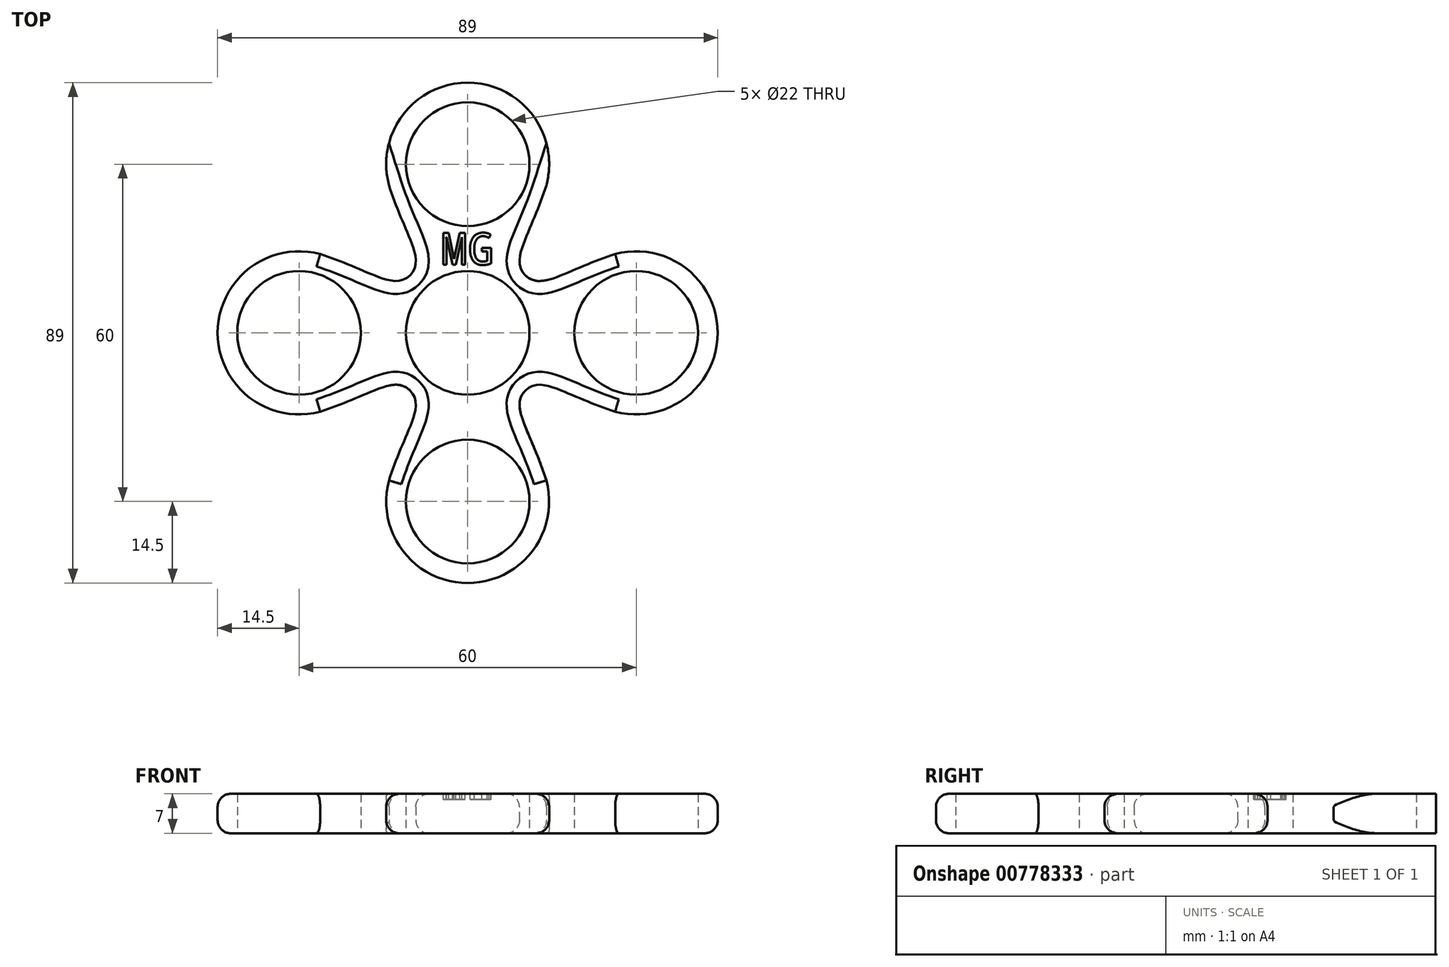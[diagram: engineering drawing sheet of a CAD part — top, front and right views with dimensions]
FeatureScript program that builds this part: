
annotation { "Feature Type Name" : "Feature", "Feature Type Description" : "" }
export const myFeature = defineFeature(function(context is Context, id is Id, definition is map)
    precondition{}
    {
        {
            var Q0;
            Q0=qCreatedBy(makeId("Top.planeOp"),FACE);
            var sketch = newSketch(context, id + "F0", { "sketchPlane" : qUnion([Q0])});
            skCircle(sketch, "E0", {"center": v(0, 0) * mm, "radius": 11 * mm});
            skCircle(sketch, "E1", {"center": v(0, 30) * mm, "radius": 11 * mm});
            skCircle(sketch, "E2", {"center": v(0, -30) * mm, "radius": 11 * mm});
            skCircle(sketch, "E3", {"center": v(30, 0) * mm, "radius": 11 * mm});
            skCircle(sketch, "E4", {"center": v(-30, 0) * mm, "radius": 11 * mm});
            skLineSegment(sketch, "E5", {"start": v(0, 0) * mm, "end": v(-49.5, 49.5) * mm, "construction": true});
            skLineSegment(sketch, "E6.MirrorCS", {"start": v(0, 0) * mm, "end": v(49.5, 49.5) * mm, "construction": true});
            skLineSegment(sketch, "E7.MirrorCS", {"start": v(0, 0) * mm, "end": v(49.5, -49.5) * mm, "construction": true});
            skLineSegment(sketch, "E8.MirrorCS", {"start": v(0, 0) * mm, "end": v(-49.5, -49.5) * mm, "construction": true});
            skArc(sketch, "E9", {"start": v(14, 26.25) * mm, "mid": v(0, 44.5) * mm, "end": v(-14, 26.25) * mm});
            skArc(sketch, "E10", {"start": v(26.25, -14) * mm, "mid": v(44.5, 0) * mm, "end": v(26.25, 14) * mm});
            skArc(sketch, "E11", {"start": v(-14, -26.25) * mm, "mid": v(0, -44.5) * mm, "end": v(14, -26.25) * mm});
            skArc(sketch, "E12", {"start": v(-26.25, 14) * mm, "mid": v(-44.5, 0) * mm, "end": v(-26.25, -14) * mm});
            skCircle(sketch, "E13", {"center": v(0, 0) * mm, "radius": 14.5 * mm, "construction": true});
            skLineSegment(sketch, "E14", {"start": v(0, 30) * mm, "end": v(-30, 0) * mm, "construction": true});
            skLineSegment(sketch, "E15", {"start": v(0, 30) * mm, "end": v(30, 0) * mm, "construction": true});
            skLineSegment(sketch, "E16", {"start": v(30, 0) * mm, "end": v(0, -30) * mm, "construction": true});
            skLineSegment(sketch, "E17", {"start": v(0, -30) * mm, "end": v(-30, 0) * mm, "construction": true});
            skFitSpline(sketch, "E18", {"points": [v(-14, 26.25) * mm, v(-10.25, 10.25) * mm], "startDerivative": vector(8.68, -26.95) * mm, "endDerivative": vector(-8.59, -8.59) * mm});
            skLineSegment(sketch, "E19", {"start": v(-10.25, 10.25) * mm, "end": v(-5.17, 15.34) * mm, "construction": true});
            skFitSpline(sketch, "E20.MirrorCS", {"points": [v(-26.25, 14) * mm, v(-10.25, 10.25) * mm], "startDerivative": vector(26.95, -8.68) * mm, "endDerivative": vector(8.59, 8.59) * mm});
            skFitSpline(sketch, "E21.MirrorCS", {"points": [v(14, 26.25) * mm, v(10.25, 10.25) * mm], "startDerivative": vector(-8.68, -26.95) * mm, "endDerivative": vector(8.59, -8.59) * mm});
            skArc(sketch, "E22.MirrorC", {"start": v(-14, 26.25) * mm, "mid": v(0, 44.5) * mm, "end": v(14, 26.25) * mm});
            skFitSpline(sketch, "E23.MirrorCS", {"points": [v(26.25, 14) * mm, v(10.25, 10.25) * mm], "startDerivative": vector(-26.95, -8.68) * mm, "endDerivative": vector(-8.59, 8.59) * mm});
            skFitSpline(sketch, "E24.MirrorCS", {"points": [v(26.25, -14) * mm, v(10.25, -10.25) * mm], "startDerivative": vector(-26.95, 8.68) * mm, "endDerivative": vector(-8.59, -8.59) * mm});
            skFitSpline(sketch, "E25.MirrorCS", {"points": [v(14, -26.25) * mm, v(10.25, -10.25) * mm], "startDerivative": vector(-8.68, 26.95) * mm, "endDerivative": vector(8.59, 8.59) * mm});
            skFitSpline(sketch, "E26.MirrorCS", {"points": [v(-14, -26.25) * mm, v(-10.25, -10.25) * mm], "startDerivative": vector(8.68, 26.95) * mm, "endDerivative": vector(-8.59, 8.59) * mm});
            skFitSpline(sketch, "E27.MirrorCS", {"points": [v(-26.25, -14) * mm, v(-10.25, -10.25) * mm], "startDerivative": vector(26.95, 8.68) * mm, "endDerivative": vector(8.59, -8.59) * mm});
            skSolve(sketch);
        }
        {
            var Q0;
            Q0=makeQuery(id+"F0.imprint","IMPRINT",FACE,{"disambiguationData":[TD([[makeQuery(id+"F0.imprint","IMPRINT",EDGE,{"derivedFrom":sQuery(id+"F0.wireOp",EDGE,"E0")}),-1.0]])]});
            extrude(context, id + "F1", {"entities" : qUnion([Q0]), "depth" : 7 * mm, "offsetDistance" : 25 * mm});
        }
        {
            var Q0;
            Q0=makeQuery(id+"F1.opExtrude","CAP_EDGE",EDGE,{"disambiguationData":[OSD([sQuery(id+"F0.wireOp",EDGE,"E27.MirrorCS")])],"isStart":false});
            var Q1;
            Q1=makeQuery(id+"F1.opExtrude","CAP_EDGE",EDGE,{"disambiguationData":[OSD([sQuery(id+"F0.wireOp",EDGE,"E20.MirrorCS")])],"isStart":false});
            var Q2;
            Q2=makeQuery(id+"F1.opExtrude","CAP_EDGE",EDGE,{"disambiguationData":[OSD([sQuery(id+"F0.wireOp",EDGE,"E12")])],"isStart":false});
            var Q3;
            Q3=makeQuery(id+"F1.opExtrude","CAP_EDGE",EDGE,{"disambiguationData":[OSD([sQuery(id+"F0.wireOp",EDGE,"E18")])],"isStart":false});
            var Q4;
            Q4=makeQuery(id+"F1.opExtrude","CAP_EDGE",EDGE,{"disambiguationData":[OSD([sQuery(id+"F0.wireOp",EDGE,"E21.MirrorCS")])],"isStart":false});
            var Q5;
            Q5=makeQuery(id+"F1.opExtrude","CAP_EDGE",EDGE,{"disambiguationData":[OSD([sQuery(id+"F0.wireOp",EDGE,"E23.MirrorCS")])],"isStart":false});
            var Q6;
            Q6=makeQuery(id+"F1.opExtrude","CAP_EDGE",EDGE,{"disambiguationData":[OSD([sQuery(id+"F0.wireOp",EDGE,"E24.MirrorCS")])],"isStart":false});
            var Q7;
            Q7=makeQuery(id+"F1.opExtrude","CAP_EDGE",EDGE,{"disambiguationData":[OSD([sQuery(id+"F0.wireOp",EDGE,"E25.MirrorCS")])],"isStart":false});
            var Q8;
            Q8=makeQuery(id+"F1.opExtrude","CAP_EDGE",EDGE,{"disambiguationData":[OSD([sQuery(id+"F0.wireOp",EDGE,"E10")])],"isStart":false});
            var Q9;
            Q9=makeQuery(id+"F1.opExtrude","CAP_EDGE",EDGE,{"disambiguationData":[OSD([sQuery(id+"F0.wireOp",EDGE,"E22.MirrorC")])],"isStart":false});
            var Q10;
            Q10=makeQuery(id+"F1.opExtrude","CAP_EDGE",EDGE,{"disambiguationData":[OSD([sQuery(id+"F0.wireOp",EDGE,"E26.MirrorCS")])],"isStart":false});
            var Q11;
            Q11=makeQuery(id+"F1.opExtrude","CAP_EDGE",EDGE,{"disambiguationData":[OSD([sQuery(id+"F0.wireOp",EDGE,"E11")])],"isStart":false});
            var Q12;
            Q12=makeQuery(id+"F1.opExtrude","CAP_EDGE",EDGE,{"disambiguationData":[OSD([sQuery(id+"F0.wireOp",EDGE,"E23.MirrorCS")])],"isStart":true});
            var Q13;
            Q13=makeQuery(id+"F1.opExtrude","CAP_EDGE",EDGE,{"disambiguationData":[OSD([sQuery(id+"F0.wireOp",EDGE,"E10")])],"isStart":true});
            var Q14;
            Q14=makeQuery(id+"F1.opExtrude","CAP_EDGE",EDGE,{"disambiguationData":[OSD([sQuery(id+"F0.wireOp",EDGE,"E24.MirrorCS")])],"isStart":true});
            var Q15;
            Q15=makeQuery(id+"F1.opExtrude","CAP_EDGE",EDGE,{"disambiguationData":[OSD([sQuery(id+"F0.wireOp",EDGE,"E25.MirrorCS")])],"isStart":true});
            var Q16;
            Q16=makeQuery(id+"F1.opExtrude","CAP_EDGE",EDGE,{"disambiguationData":[OSD([sQuery(id+"F0.wireOp",EDGE,"E11")])],"isStart":true});
            var Q17;
            Q17=makeQuery(id+"F1.opExtrude","CAP_EDGE",EDGE,{"disambiguationData":[OSD([sQuery(id+"F0.wireOp",EDGE,"E26.MirrorCS")])],"isStart":true});
            var Q18;
            Q18=makeQuery(id+"F1.opExtrude","CAP_EDGE",EDGE,{"disambiguationData":[OSD([sQuery(id+"F0.wireOp",EDGE,"E27.MirrorCS")])],"isStart":true});
            var Q19;
            Q19=makeQuery(id+"F1.opExtrude","CAP_EDGE",EDGE,{"disambiguationData":[OSD([sQuery(id+"F0.wireOp",EDGE,"E12")])],"isStart":true});
            var Q20;
            Q20=makeQuery(id+"F1.opExtrude","CAP_EDGE",EDGE,{"disambiguationData":[OSD([sQuery(id+"F0.wireOp",EDGE,"E20.MirrorCS")])],"isStart":true});
            var Q21;
            Q21=makeQuery(id+"F1.opExtrude","CAP_EDGE",EDGE,{"disambiguationData":[OSD([sQuery(id+"F0.wireOp",EDGE,"E18")])],"isStart":true});
            var Q22;
            Q22=makeQuery(id+"F1.opExtrude","CAP_EDGE",EDGE,{"disambiguationData":[OSD([sQuery(id+"F0.wireOp",EDGE,"E22.MirrorC")])],"isStart":true});
            var Q23;
            Q23=makeQuery(id+"F1.opExtrude","CAP_EDGE",EDGE,{"disambiguationData":[OSD([sQuery(id+"F0.wireOp",EDGE,"E21.MirrorCS")])],"isStart":true});
            fillet(context, id + "F2", {"entities" : qUnion([Q0, Q1, Q2, Q3, Q4, Q5, Q6, Q7, Q8, Q9, Q10, Q11, Q12, Q13, Q14, Q15, Q16, Q17, Q18, Q19, Q20, Q21, Q22, Q23]), "radius" : 2.3 * mm, "tangentPropagation" : true, "allowEdgeOverflow" : false});
        }
        {
            var Q0;
            Q0=makeQuery(id+"F1.opExtrude","CAP_FACE",FACE,{"disambiguationData":[OSD([sQuery(id+"F0.wireOp",EDGE,"E0"),sQuery(id+"F0.wireOp",EDGE,"E1"),sQuery(id+"F0.wireOp",EDGE,"E2"),sQuery(id+"F0.wireOp",EDGE,"E3"),sQuery(id+"F0.wireOp",EDGE,"E4"),sQuery(id+"F0.wireOp",EDGE,"E10"),sQuery(id+"F0.wireOp",EDGE,"E11"),sQuery(id+"F0.wireOp",EDGE,"E12"),sQuery(id+"F0.wireOp",EDGE,"E18"),sQuery(id+"F0.wireOp",EDGE,"E20.MirrorCS"),sQuery(id+"F0.wireOp",EDGE,"E21.MirrorCS"),sQuery(id+"F0.wireOp",EDGE,"E22.MirrorC"),sQuery(id+"F0.wireOp",EDGE,"E23.MirrorCS"),sQuery(id+"F0.wireOp",EDGE,"E24.MirrorCS"),sQuery(id+"F0.wireOp",EDGE,"E25.MirrorCS"),sQuery(id+"F0.wireOp",EDGE,"E26.MirrorCS"),sQuery(id+"F0.wireOp",EDGE,"E27.MirrorCS")])],"isStart":false});
            var sketch = newSketch(context, id + "F3", { "sketchPlane" : qUnion([Q0])});
            skText(sketch, "E28", { "text": "MG", "fontName": "DroidSansMono.ttf"});
            const initialGuessF3  = {"E28": [-0.00476, 0.01213, 1, 0, 0.00567]};
            skSetInitialGuess(sketch, initialGuessF3);
            skSolve(sketch);
        }
        {
            var Q0;
            Q0 = qSketchRegion(id + "F3", true);
            extrude(context, id + "F4", {"entities" : qUnion([Q0]), "operationType" : NewBodyOperationType.REMOVE, "oppositeDirection" : true, "depth" : 1 * mm, "offsetDistance" : 25 * mm});
        }
    });
